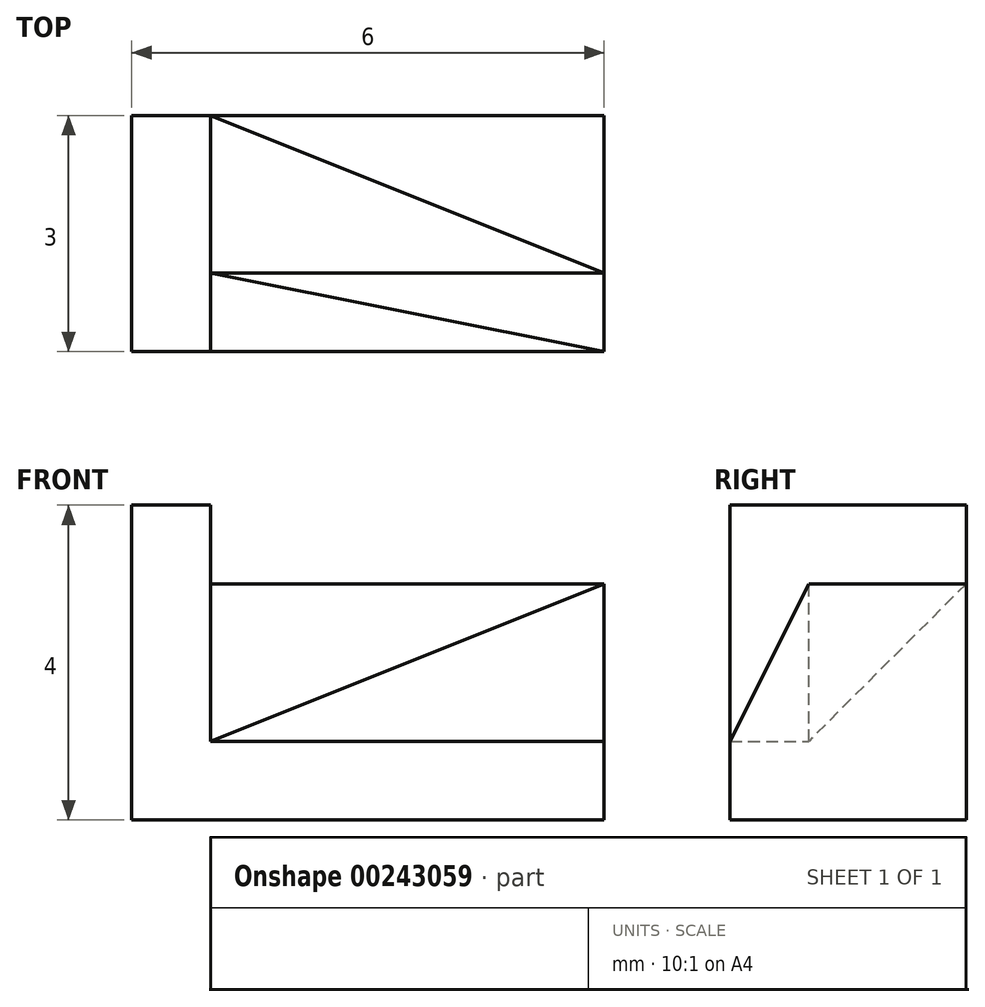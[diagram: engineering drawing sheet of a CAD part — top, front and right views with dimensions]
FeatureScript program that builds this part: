
annotation { "Feature Type Name" : "Feature", "Feature Type Description" : "" }
export const myFeature = defineFeature(function(context is Context, id is Id, definition is map)
    precondition{}
    {
        {
            var Q0;
            Q0=qCreatedBy(makeId("Front.planeOp"),FACE);
            var sketch = newSketch(context, id + "F0", { "sketchPlane" : qUnion([Q0])});
            skLineSegment(sketch, "E0.bottom", {"start": v(0, 0) * mm, "end": v(5, 0) * mm});
            skLineSegment(sketch, "E0.top", {"start": v(0, 3) * mm, "end": v(5, 3) * mm});
            skLineSegment(sketch, "E0.left", {"start": v(0, 0) * mm, "end": v(0, 3) * mm});
            skLineSegment(sketch, "E0.right", {"start": v(5, 0) * mm, "end": v(5, 3) * mm});
            skSolve(sketch);
        }
        {
            var Q0;
            Q0 = qSketchRegion(id + "F0", true);
            extrude(context, id + "F1", {"entities" : qUnion([Q0]), "oppositeDirection" : true, "depth" : 3 * mm});
        }
        {
            var Q0;
            Q0=makeQuery(id+"F1.opExtrude","SWEPT_FACE",FACE,{"disambiguationData":[OSD([sQuery(id+"F0.wireOp",EDGE,"E0.top")])]});
            var sketch = newSketch(context, id + "F2", { "sketchPlane" : qUnion([Q0])});
            skLineSegment(sketch, "E1", {"start": v(0, 0) * mm, "end": v(5, 0) * mm});
            skLineSegment(sketch, "E2", {"start": v(5, 0) * mm, "end": v(0, 1) * mm});
            skSolve(sketch);
        }
        {
            var Q0;
            {var subQ0=sQuery(id+"F2.wireOp",EDGE,"E1");Q0=makeQuery(id+"F2.imprint","IMPRINT",FACE,{"disambiguationData":[TD([[makeQuery(id+"F2.imprint","IMPRINT",EDGE,{"derivedFrom":subQ0}),1.0]])]});}
            extrude(context, id + "F3", {"entities" : qUnion([Q0]), "operationType" : NewBodyOperationType.REMOVE, "oppositeDirection" : true, "depth" : 2 * mm});
        }
        {
            var Q0;
            Q0=makeQuery(id+"F1.opExtrude","SWEPT_FACE",FACE,{"disambiguationData":[OSD([sQuery(id+"F0.wireOp",EDGE,"E0.right")])]});
            var sketch = newSketch(context, id + "F4", { "sketchPlane" : qUnion([Q0])});
            skLineSegment(sketch, "E3", {"start": v(0, 0) * mm, "end": v(1, 0) * mm, "construction": true});
            skLineSegment(sketch, "E4", {"start": v(1, 0) * mm, "end": v(1, 3) * mm, "construction": true});
            skSolve(sketch);
        }
        {
            var Q0;
            Q0=makeQuery(id+"F3.boolean.opBoolean","COPY",VERTEX,{"derivedFrom":makeQuery(id+"F3.opExtrude","CAP_VERTEX",VERTEX,{"disambiguationData":[OSD([sQuery(id+"F0.wireOp",EDGE,"E0.top"),sQuery(id+"F0.wireOp",EDGE,"E0.left"),sQuery(id+"F2.wireOp",EDGE,"E2")])],"isStart":false})});
            var Q1;
            Q1=makeQuery(id+"F3.boolean.opBoolean","COPY",VERTEX,{"derivedFrom":makeQuery(id+"F3.opExtrude","CAP_VERTEX",VERTEX,{"disambiguationData":[OSD([sQuery(id+"F0.wireOp",EDGE,"E0.top"),sQuery(id+"F0.wireOp",EDGE,"E0.right"),sQuery(id+"F2.wireOp",EDGE,"E1"),sQuery(id+"F2.wireOp",EDGE,"E2")])],"isStart":false})});
            var Q2;
            Q2=sQuery(id+"F4.wireOp",VERTEX,"E4.end");
            cPlane(context, id + "F5", {"entities" : qUnion([Q0, Q1, Q2]), "cplaneType" : CPlaneType.THREE_POINT, "offset" : 25 * mm, "width" : 150 * mm, "height" : 150 * mm});
        }
        {
            var Q0;
            Q0=qCreatedBy(id+"F5.planeOp",FACE);
            var sketch = newSketch(context, id + "F6", { "sketchPlane" : qUnion([Q0])});
            skPoint(sketch, "E5.0", {"position": v(0.08, 1.34) * mm});
            skPoint(sketch, "E6.0", {"position": v(-5, 0.9) * mm});
            skPoint(sketch, "E7.0", {"position": v(-5, 3.13) * mm});
            skLineSegment(sketch, "E8", {"start": v(0.08, 1.34) * mm, "end": v(-5, 3.13) * mm});
            skLineSegment(sketch, "E9", {"start": v(-5, 0.9) * mm, "end": v(0.08, 1.34) * mm});
            skLineSegment(sketch, "E10", {"start": v(-5, 3.13) * mm, "end": v(-6.2, 3.13) * mm});
            skLineSegment(sketch, "E11", {"start": v(-5, 0.9) * mm, "end": v(-6.22, 0.9) * mm});
            skLineSegment(sketch, "E12", {"start": v(-6.22, 0.9) * mm, "end": v(-6.2, 3.13) * mm});
            skSolve(sketch);
        }
        {
            var Q0;
            Q0 = qSketchRegion(id + "F6", true);
            extrude(context, id + "F7", {"entities" : qUnion([Q0]), "operationType" : NewBodyOperationType.REMOVE, "oppositeDirection" : true, "depth" : 25 * mm});
        }
        {
            var Q0;
            Q0=makeQuery(id+"F7.boolean.opBoolean","MERGE",VERTEX,{"derivedFrom":[makeQuery(id+"F3.boolean.opBoolean","COPY",VERTEX,{"derivedFrom":makeQuery(id+"F3.opExtrude","CAP_VERTEX",VERTEX,{"disambiguationData":[OSD([sQuery(id+"F0.wireOp",EDGE,"E0.top"),sQuery(id+"F0.wireOp",EDGE,"E0.left"),sQuery(id+"F2.wireOp",EDGE,"E2")])],"isStart":false})}),makeQuery(id+"F7.opExtrude","CAP_VERTEX",VERTEX,{"disambiguationData":[OSD([sQuery(id+"F6.wireOp",EDGE,"E8"),sQuery(id+"F6.wireOp",EDGE,"E9")])],"isStart":true})]});
            var Q1;
            Q1=sQuery(id+"F4.wireOp",VERTEX,"E4.end");
            var Q2;
            Q2=makeQuery(id+"F1.opExtrude","CAP_VERTEX",VERTEX,{"disambiguationData":[OSD([sQuery(id+"F0.wireOp",EDGE,"E0.top"),sQuery(id+"F0.wireOp",EDGE,"E0.left")])],"isStart":false});
            cPlane(context, id + "F8", {"entities" : qUnion([Q0, Q1, Q2]), "cplaneType" : CPlaneType.THREE_POINT, "offset" : 25 * mm, "width" : 150 * mm, "height" : 150 * mm});
        }
        {
            var Q0;
            Q0=qCreatedBy(id+"F8.planeOp",FACE);
            var sketch = newSketch(context, id + "F9", { "sketchPlane" : qUnion([Q0])});
            skPoint(sketch, "E13.0", {"position": v(-5.2, 2.83) * mm});
            skPoint(sketch, "E14.0", {"position": v(0, 4.24) * mm});
            skPoint(sketch, "E15.0", {"position": v(0, 1.41) * mm});
            skLineSegment(sketch, "E16", {"start": v(0, 4.24) * mm, "end": v(-5.2, 2.83) * mm});
            skLineSegment(sketch, "E17", {"start": v(0, 4.24) * mm, "end": v(0, 1.41) * mm});
            skLineSegment(sketch, "E18", {"start": v(-5.2, 2.83) * mm, "end": v(-5.48, 1.77) * mm});
            skLineSegment(sketch, "E19", {"start": v(-5.48, 1.77) * mm, "end": v(0, 1.41) * mm});
            skSolve(sketch);
        }
        {
            var Q0;
            Q0 = qSketchRegion(id + "F9", true);
            extrude(context, id + "F10", {"entities" : qUnion([Q0]), "operationType" : NewBodyOperationType.REMOVE, "oppositeDirection" : true, "depth" : 25 * mm});
        }
        {
            var Q0;
            Q0=qCreatedBy(makeId("Front.planeOp"),FACE);
            var sketch = newSketch(context, id + "F11", { "sketchPlane" : qUnion([Q0])});
            skLineSegment(sketch, "E20", {"start": v(0, 0) * mm, "end": v(-1, 0) * mm});
            skLineSegment(sketch, "E21", {"start": v(-1, 0) * mm, "end": v(-1, 4) * mm});
            skLineSegment(sketch, "E22", {"start": v(-1, 4) * mm, "end": v(0, 4) * mm});
            skLineSegment(sketch, "E23", {"start": v(0, 4) * mm, "end": v(0, 0) * mm});
            skSolve(sketch);
        }
        {
            var Q0;
            Q0=makeQuery(id+"F11.imprint","IMPRINT",FACE,{"disambiguationData":[TD([[makeQuery(id+"F11.imprint","IMPRINT",EDGE,{"derivedFrom":sQuery(id+"F11.wireOp",EDGE,"E20")}),-1.0]])]});
            extrude(context, id + "F12", {"entities" : qUnion([Q0]), "operationType" : NewBodyOperationType.ADD, "oppositeDirection" : true, "depth" : 3 * mm});
        }
    });
